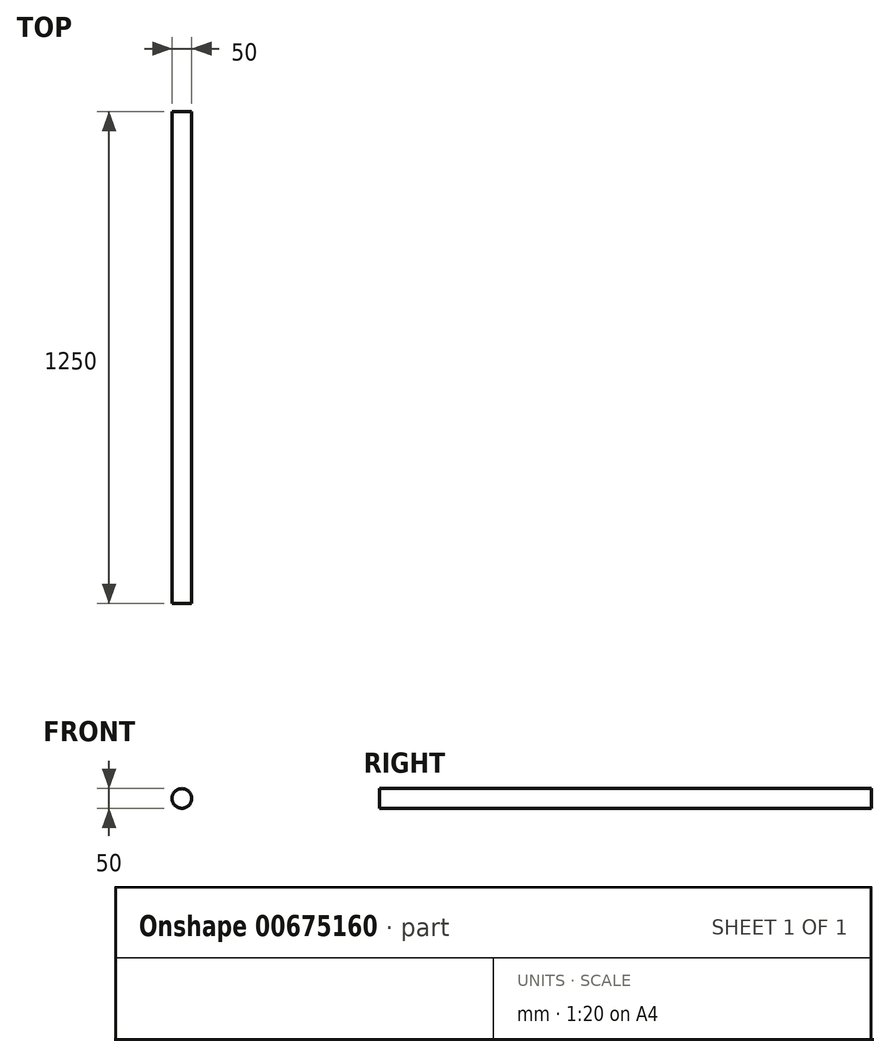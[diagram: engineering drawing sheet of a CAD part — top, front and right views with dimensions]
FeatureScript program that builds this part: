
annotation { "Feature Type Name" : "Feature", "Feature Type Description" : "" }
export const myFeature = defineFeature(function(context is Context, id is Id, definition is map)
    precondition{}
    {
        {
            var Q0;
            Q0=qCreatedBy(makeId("Front.planeOp"),FACE);
            var sketch = newSketch(context, id + "F0", { "sketchPlane" : qUnion([Q0])});
            skCircle(sketch, "E0", {"center": v(0, 0) * mm, "radius": 25 * mm});
            skSolve(sketch);
        }
        {
            var Q0;
            Q0=makeQuery(id+"F0.imprint","IMPRINT",FACE,{"disambiguationData":[TD([[makeQuery(id+"F0.imprint","IMPRINT",EDGE,{"derivedFrom":sQuery(id+"F0.wireOp",EDGE,"E0")}),1.0]])]});
            extrude(context, id + "F1", {"entities" : qUnion([Q0]), "depth" : 1250 * mm, "offsetDistance" : 25 * mm});
        }
    });
